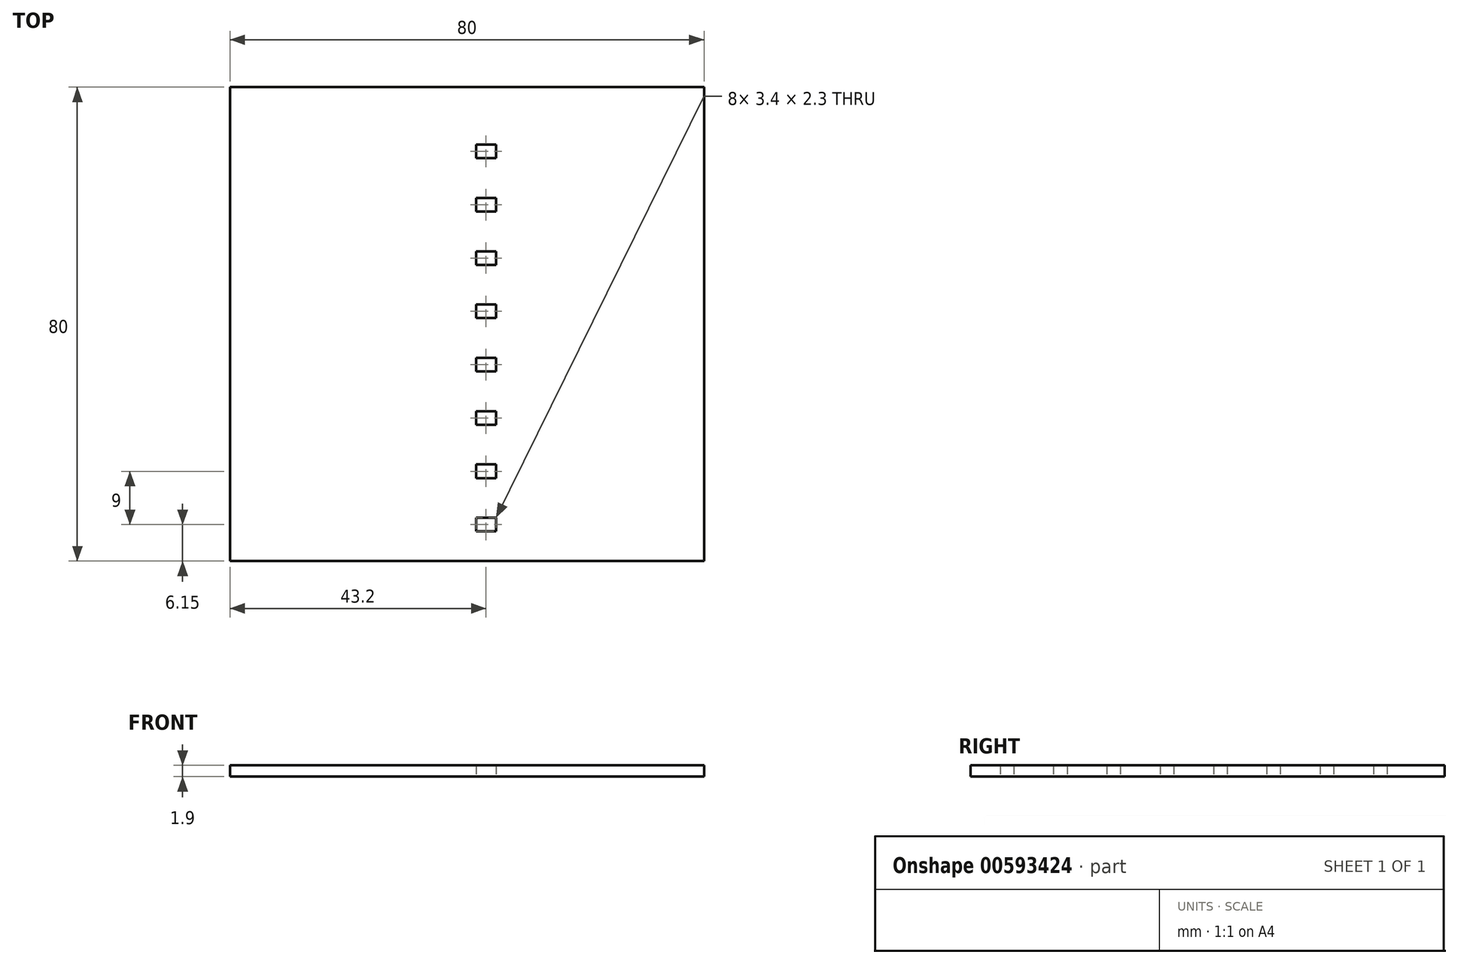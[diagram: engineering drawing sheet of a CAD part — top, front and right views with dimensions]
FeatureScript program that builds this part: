
annotation { "Feature Type Name" : "Feature", "Feature Type Description" : "" }
export const myFeature = defineFeature(function(context is Context, id is Id, definition is map)
    precondition{}
    {
        {
            var Q0;
            Q0=qCreatedBy(makeId("Top.planeOp"),FACE);
            var sketch = newSketch(context, id + "F0", { "sketchPlane" : qUnion([Q0])});
            skLineSegment(sketch, "E0.bottom", {"start": v(0, 0) * mm, "end": v(80, 0) * mm});
            skLineSegment(sketch, "E0.top", {"start": v(0, 80) * mm, "end": v(80, 80) * mm});
            skLineSegment(sketch, "E0.left", {"start": v(0, 0) * mm, "end": v(0, 80) * mm});
            skLineSegment(sketch, "E0.right", {"start": v(80, 0) * mm, "end": v(80, 80) * mm});
            skLineSegment(sketch, "E1", {"start": v(40, 80) * mm, "end": v(40, 0) * mm, "construction": true});
            skLineSegment(sketch, "E2.bottom", {"start": v(41.5, 5) * mm, "end": v(44.9, 5) * mm});
            skLineSegment(sketch, "E2.top", {"start": v(41.5, 7.3) * mm, "end": v(44.9, 7.3) * mm});
            skLineSegment(sketch, "E2.left", {"start": v(41.5, 5) * mm, "end": v(41.5, 7.3) * mm});
            skLineSegment(sketch, "E2.right", {"start": v(44.9, 5) * mm, "end": v(44.9, 7.3) * mm});
            skLineSegment(sketch, "E3.0.1.0", {"start": v(44.9, 14) * mm, "end": v(44.9, 16.3) * mm});
            skLineSegment(sketch, "E3.0.1.1", {"start": v(41.5, 14) * mm, "end": v(41.5, 16.3) * mm});
            skLineSegment(sketch, "E3.0.1.2", {"start": v(41.5, 16.3) * mm, "end": v(44.9, 16.3) * mm});
            skLineSegment(sketch, "E3.0.1.3", {"start": v(41.5, 14) * mm, "end": v(44.9, 14) * mm});
            skLineSegment(sketch, "E3.0.2.0", {"start": v(44.9, 23) * mm, "end": v(44.9, 25.3) * mm});
            skLineSegment(sketch, "E3.0.2.1", {"start": v(41.5, 23) * mm, "end": v(41.5, 25.3) * mm});
            skLineSegment(sketch, "E3.0.2.2", {"start": v(41.5, 25.3) * mm, "end": v(44.9, 25.3) * mm});
            skLineSegment(sketch, "E3.0.2.3", {"start": v(41.5, 23) * mm, "end": v(44.9, 23) * mm});
            skLineSegment(sketch, "E3.0.3.0", {"start": v(44.9, 32) * mm, "end": v(44.9, 34.3) * mm});
            skLineSegment(sketch, "E3.0.3.1", {"start": v(41.5, 32) * mm, "end": v(41.5, 34.3) * mm});
            skLineSegment(sketch, "E3.0.3.2", {"start": v(41.5, 34.3) * mm, "end": v(44.9, 34.3) * mm});
            skLineSegment(sketch, "E3.0.3.3", {"start": v(41.5, 32) * mm, "end": v(44.9, 32) * mm});
            skLineSegment(sketch, "E3.0.4.0", {"start": v(44.9, 41) * mm, "end": v(44.9, 43.3) * mm});
            skLineSegment(sketch, "E3.0.4.1", {"start": v(41.5, 41) * mm, "end": v(41.5, 43.3) * mm});
            skLineSegment(sketch, "E3.0.4.2", {"start": v(41.5, 43.3) * mm, "end": v(44.9, 43.3) * mm});
            skLineSegment(sketch, "E3.0.4.3", {"start": v(41.5, 41) * mm, "end": v(44.9, 41) * mm});
            skLineSegment(sketch, "E3.0.5.0", {"start": v(44.9, 50) * mm, "end": v(44.9, 52.3) * mm});
            skLineSegment(sketch, "E3.0.5.1", {"start": v(41.5, 50) * mm, "end": v(41.5, 52.3) * mm});
            skLineSegment(sketch, "E3.0.5.2", {"start": v(41.5, 52.3) * mm, "end": v(44.9, 52.3) * mm});
            skLineSegment(sketch, "E3.0.5.3", {"start": v(41.5, 50) * mm, "end": v(44.9, 50) * mm});
            skLineSegment(sketch, "E3.0.6.0", {"start": v(44.9, 59) * mm, "end": v(44.9, 61.3) * mm});
            skLineSegment(sketch, "E3.0.6.1", {"start": v(41.5, 59) * mm, "end": v(41.5, 61.3) * mm});
            skLineSegment(sketch, "E3.0.6.2", {"start": v(41.5, 61.3) * mm, "end": v(44.9, 61.3) * mm});
            skLineSegment(sketch, "E3.0.6.3", {"start": v(41.5, 59) * mm, "end": v(44.9, 59) * mm});
            skLineSegment(sketch, "E3.0.7.0", {"start": v(44.9, 68) * mm, "end": v(44.9, 70.3) * mm});
            skLineSegment(sketch, "E3.0.7.1", {"start": v(41.5, 68) * mm, "end": v(41.5, 70.3) * mm});
            skLineSegment(sketch, "E3.0.7.2", {"start": v(41.5, 70.3) * mm, "end": v(44.9, 70.3) * mm});
            skLineSegment(sketch, "E3.0.7.3", {"start": v(41.5, 68) * mm, "end": v(44.9, 68) * mm});
            skLineSegment(sketch, "E3.direction1", {"start": v(41.5, 5) * mm, "end": v(66.5, 5) * mm, "construction": true});
            skLineSegment(sketch, "E3.direction2", {"start": v(41.5, 5) * mm, "end": v(41.5, 14) * mm, "construction": true});
            skSolve(sketch);
        }
        {
            var Q0;
            Q0 = qSketchRegion(id + "F0", true);
            extrude(context, id + "F1", {"entities" : qUnion([Q0]), "depth" : 1.9 * mm, "offsetDistance" : 25 * mm});
        }
    });
